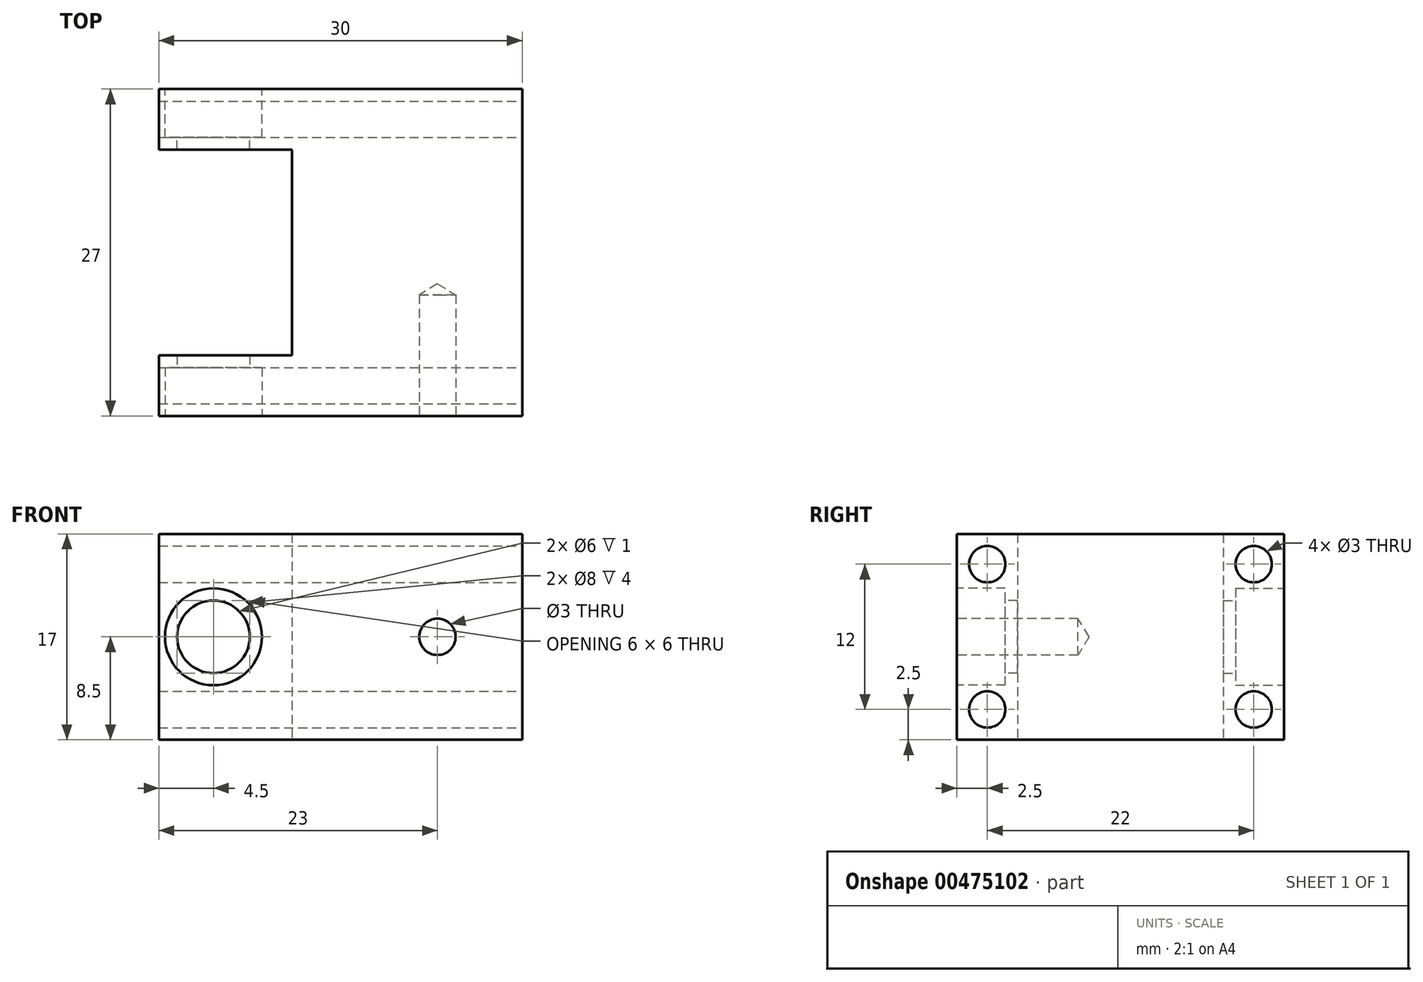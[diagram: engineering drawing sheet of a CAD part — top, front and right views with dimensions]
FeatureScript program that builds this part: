
annotation { "Feature Type Name" : "Feature", "Feature Type Description" : "" }
export const myFeature = defineFeature(function(context is Context, id is Id, definition is map)
    precondition{}
    {
        {
            var Q0;
            Q0=qCreatedBy(makeId("Top.planeOp"),FACE);
            var sketch = newSketch(context, id + "F0", { "sketchPlane" : qUnion([Q0])});
            skLineSegment(sketch, "E0", {"start": v(-11, 13.5) * mm, "end": v(19, 13.5) * mm});
            skLineSegment(sketch, "E1", {"start": v(19, 13.5) * mm, "end": v(19, -13.5) * mm});
            skLineSegment(sketch, "E2", {"start": v(19, -13.5) * mm, "end": v(-11, -13.5) * mm});
            skLineSegment(sketch, "E3", {"start": v(-11, -13.5) * mm, "end": v(-11, -8.5) * mm});
            skLineSegment(sketch, "E4", {"start": v(-11, -8.5) * mm, "end": v(0, -8.5) * mm});
            skLineSegment(sketch, "E5", {"start": v(0, -8.5) * mm, "end": v(0, 8.5) * mm});
            skLineSegment(sketch, "E6", {"start": v(0, 8.5) * mm, "end": v(-11, 8.5) * mm});
            skLineSegment(sketch, "E7", {"start": v(-11, 8.5) * mm, "end": v(-11, 13.5) * mm});
            skSolve(sketch);
        }
        {
            var Q0;
            Q0=makeQuery(id+"F0.imprint","IMPRINT",FACE,{"disambiguationData":[TD([[makeQuery(id+"F0.imprint","IMPRINT",EDGE,{"derivedFrom":sQuery(id+"F0.wireOp",EDGE,"E0")}),-1.0]])]});
            extrude(context, id + "F1", {"entities" : qUnion([Q0]), "endBound" : BoundingType.SYMMETRIC, "depth" : 17 * mm});
        }
        {
            var Q0;
            Q0=makeQuery(id+"F1.opExtrude","SWEPT_FACE",FACE,{"disambiguationData":[OSD([sQuery(id+"F0.wireOp",EDGE,"E2")])]});
            var sketch = newSketch(context, id + "F2", { "sketchPlane" : qUnion([Q0])});
            skCircle(sketch, "E8", {"center": v(-6.5, 0) * mm, "radius": 4 * mm});
            skCircle(sketch, "E9.0", {"center": v(-6.5, 0) * mm, "radius": 3 * mm});
            skPoint(sketch, "E10", {"position": v(12, 0) * mm});
            skSolve(sketch);
        }
        {
            var Q0;
            Q0=makeQuery(id+"F2.imprint","IMPRINT",FACE,{"disambiguationData":[TD([[makeQuery(id+"F2.imprint","IMPRINT",EDGE,{"derivedFrom":sQuery(id+"F2.wireOp",EDGE,"E9.0")}),1.0]])]});
            var Q1;
            Q1=makeQuery(id+"F1.opExtrude","SWEPT_FACE",FACE,{"disambiguationData":[OSD([sQuery(id+"F0.wireOp",EDGE,"E4")])]});
            extrude(context, id + "F3", {"entities" : qUnion([Q0]), "operationType" : NewBodyOperationType.REMOVE, "endBound" : BoundingType.UP_TO_SURFACE, "oppositeDirection" : true, "endBoundEntityFace" : qUnion([Q1]), "depth" : 25 * mm});
        }
        {
            var Q0;
            Q0=makeQuery(id+"F2.imprint","IMPRINT",FACE,{"disambiguationData":[TD([[makeQuery(id+"F2.imprint","IMPRINT",EDGE,{"derivedFrom":sQuery(id+"F2.wireOp",EDGE,"E8")}),1.0]])]});
            extrude(context, id + "F4", {"entities" : qUnion([Q0]), "operationType" : NewBodyOperationType.REMOVE, "oppositeDirection" : true, "depth" : 4 * mm});
        }
        {
            var Q0;
            Q0=makeQuery(id+"F1.opExtrude","SWEPT_FACE",FACE,{"disambiguationData":[OSD([sQuery(id+"F0.wireOp",EDGE,"E0")])]});
            var sketch = newSketch(context, id + "F5", { "sketchPlane" : qUnion([Q0])});
            skCircle(sketch, "E11", {"center": v(6.5, 0) * mm, "radius": 4 * mm});
            skCircle(sketch, "E12.0", {"center": v(6.5, 0) * mm, "radius": 3 * mm});
            skSolve(sketch);
        }
        {
            var Q0;
            Q0=makeQuery(id+"F5.imprint","IMPRINT",FACE,{"disambiguationData":[TD([[makeQuery(id+"F5.imprint","IMPRINT",EDGE,{"derivedFrom":sQuery(id+"F5.wireOp",EDGE,"E12.0")}),1.0]])]});
            var Q1;
            Q1=makeQuery(id+"F1.opExtrude","SWEPT_FACE",FACE,{"disambiguationData":[OSD([sQuery(id+"F0.wireOp",EDGE,"E6")])]});
            extrude(context, id + "F6", {"entities" : qUnion([Q0]), "operationType" : NewBodyOperationType.REMOVE, "endBound" : BoundingType.UP_TO_SURFACE, "oppositeDirection" : true, "endBoundEntityFace" : qUnion([Q1]), "depth" : 25 * mm});
        }
        {
            var Q0;
            Q0 = qSketchRegion(id + "F5", true);
            extrude(context, id + "F7", {"entities" : qUnion([Q0]), "operationType" : NewBodyOperationType.REMOVE, "oppositeDirection" : true, "depth" : 4 * mm});
        }
        {
            var Q0;
            Q0=makeQuery(id+"F1.opExtrude","SWEPT_FACE",FACE,{"disambiguationData":[OSD([sQuery(id+"F0.wireOp",EDGE,"E1")])]});
            var sketch = newSketch(context, id + "F8", { "sketchPlane" : qUnion([Q0])});
            skPoint(sketch, "E13", {"position": v(-11, 6) * mm});
            skPoint(sketch, "E14.MirrorP", {"position": v(11, 6) * mm});
            skPoint(sketch, "E15.MirrorP", {"position": v(11, -6) * mm});
            skPoint(sketch, "E16.MirrorP", {"position": v(-11, -6) * mm});
            skSolve(sketch);
        }
        {
            var Q0;
            Q0=sQuery(id+"F8.wireOp",VERTEX,"E13");
            var Q1;
            Q1=sQuery(id+"F8.wireOp",VERTEX,"E16.MirrorP");
            var Q2;
            Q2=sQuery(id+"F8.wireOp",VERTEX,"E15.MirrorP");
            var Q3;
            Q3=sQuery(id+"F8.wireOp",VERTEX,"E14.MirrorP");
            var Q4;
            Q4=makeQuery(id+"F1.opExtrude","SWEPT_BODY",BODY,{"disambiguationData":[OSD([sQuery(id+"F0.wireOp",EDGE,"E0"),sQuery(id+"F0.wireOp",EDGE,"E1"),sQuery(id+"F0.wireOp",EDGE,"E2"),sQuery(id+"F0.wireOp",EDGE,"E3"),sQuery(id+"F0.wireOp",EDGE,"E4"),sQuery(id+"F0.wireOp",EDGE,"E5"),sQuery(id+"F0.wireOp",EDGE,"E6"),sQuery(id+"F0.wireOp",EDGE,"E7")])]});
            hole(context, id + "F9", {"style" : HoleStyle.SIMPLE, "endStyle" : HoleEndStyle.THROUGH, "holeDiameter" : 3 * mm, "isTappedThrough" : true, "tappedDepth" : 12 * mm, "tapClearance" : 3, "locations" : qUnion([Q0, Q1, Q2, Q3]), "scope" : qUnion([Q4])});
        }
        {
            var Q0;
            Q0=sQuery(id+"F2.wireOp",VERTEX,"E10");
            var Q1;
            Q1=makeQuery(id+"F1.opExtrude","SWEPT_BODY",BODY,{"disambiguationData":[OSD([sQuery(id+"F0.wireOp",EDGE,"E0"),sQuery(id+"F0.wireOp",EDGE,"E1"),sQuery(id+"F0.wireOp",EDGE,"E2"),sQuery(id+"F0.wireOp",EDGE,"E3"),sQuery(id+"F0.wireOp",EDGE,"E4"),sQuery(id+"F0.wireOp",EDGE,"E5"),sQuery(id+"F0.wireOp",EDGE,"E6"),sQuery(id+"F0.wireOp",EDGE,"E7")])]});
            hole(context, id + "F10", {"style" : HoleStyle.SIMPLE, "endStyle" : HoleEndStyle.BLIND, "holeDiameter" : 3 * mm, "holeDepth" : 10 * mm, "isTappedThrough" : true, "tappedDepth" : 12 * mm, "tapClearance" : 3, "locations" : qUnion([Q0]), "scope" : qUnion([Q1])});
        }
    });
